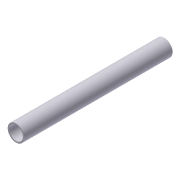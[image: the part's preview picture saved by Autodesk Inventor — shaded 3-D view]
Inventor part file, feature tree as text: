
AUTODESK INVENTOR PART (.ipt)
format: ipt  version: 2012 (Build 160160000, 160)  size: 64,000 bytes
history: native  units: in
note: dims shown in document units (in); Inventor stores cm internally (conversion verified against a paired STEP export)
features: extrude x1, sketch x1
ambient origin geometry x8: Origin, YZ Plane, XZ Plane, XY Plane, X Axis, Y Axis, Z Axis, Center Point
bodies: Solid1 (feature_tree)
feature tree (2):
  extrude  "Extrusion1"  Depth=1.375in
  sketch  "Sketch1"  dims[d0=1.656in d1=1.375in d2=14.75in d3=0.0in]
